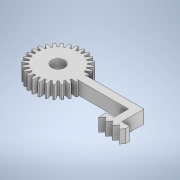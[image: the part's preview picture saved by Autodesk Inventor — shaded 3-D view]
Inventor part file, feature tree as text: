
AUTODESK INVENTOR PART (.ipt)
format: ipt  version: 2022 (Build 260153000, 153)  size: 415,232 bytes
history: native  units: in
note: dims shown in document units (in); Inventor stores cm internally (conversion verified against a paired STEP export)
features: sketch x13, extrude x12, pattern_circular x1
ambient origin geometry x8: Origin, YZ Plane, XZ Plane, XY Plane, X Axis, Y Axis, Z Axis, Center Point
bodies: Solid1 (feature_tree)
feature tree (26):
  extrude  "Extrusion1"  Depth=0.1575in
  pattern_circular  "Circular Pattern1"  Count=28 Angle=360.0deg
  extrude  "Extrusion6"  Depth=0.1969in
  extrude  "Extrusion7"  Depth=1.1811in
  extrude  "Extrusion8"  Depth=0.748in
  extrude  "Extrusion9"  Depth=0.1969in
  extrude  "Extrusion10"  Depth=0.1969in
  extrude  "Extrusion11"  Depth=0.1969in
  extrude  "Extrusion12"  Depth=0.1969in
  sketch  "Sketch17"  dims[d49=0.1969in d50=0.1575in]
  extrude  "Extrusion13"  Depth=0.3543in
  extrude  "Extrusion14"  Depth=0.1969in
  extrude  "Extrusion15"  Depth=0.1181in
  extrude  "Extrusion16"  Depth=0.1969in
  sketch  "Sketch1"  dims[d0=0.6299in d1=0.1575in]
  sketch  "Sketch8"  dims[d2=0.0098in]
  sketch  "Sketch9"  dims[d3=0.0098in]
  sketch  "Sketch10"  dims[d4=0.0236in]
  sketch  "Sketch11"  dims[d7=0.0472in]
  sketch  "Sketch14"  dims[d8=0.1772in]
  sketch  "Sketch15"  dims[d10=0.0787in]
  sketch  "Sketch16"  dims[d11=0.1969in d12=0.0in d13=11.0236in d14=360.0deg]
  sketch  "Sketch18"  dims[d51=0.5438in d52=0.0in d53=1.1811in]
  sketch  "Sketch19"  dims[d54=0.7087in d55=0.748in]
  sketch  "Sketch20"  dims[d56=0.748in d57=0.1969in]
  sketch  "Sketch21"  dims[d58=0.9843in d59=0.0591in d60=0.0591in d61=0.0591in d62=0.3543in d63=0.0591in d64=0.1181in d65=0.1969in d66=0.0197in d67=0.0197in d68=0.0197in d69=0.1969in d70=0.0in d71=1.1811in d72=0.3543in d73=0.1181in d74=0.1181in d75=0.3543in d76=0.1181in d77=0.1969in d78=0.0197in d79=0.1969in d80=0.0197in d81=0.0197in d82=0.1969in d83=0.0in d84=0.2938in d85=0.0in d93=1.1811in d94=0.3937in d95=0.9843in d96=1.2205in d97=0.3543in d98=0.1181in d99=0.1181in d100=0.0787in d101=0.1181in d102=0.0787in d103=0.1969in d104=0.0in d105=0.0787in d106=0.0787in d107=0.3031in d108=0.0in d109=0.0394in d110=0.5094in d111=0.0in d112=1.6156in d113=0.0in d114=0.9469in d115=0.0in d116=1.1811in d117=0.3937in d118=0.1181in d119=0.1181in d120=0.1181in d121=0.1181in d122=0.1969in d123=0.0in d124=0.0787in d126=0.0787in d127=0.5438in d128=0.0in]
